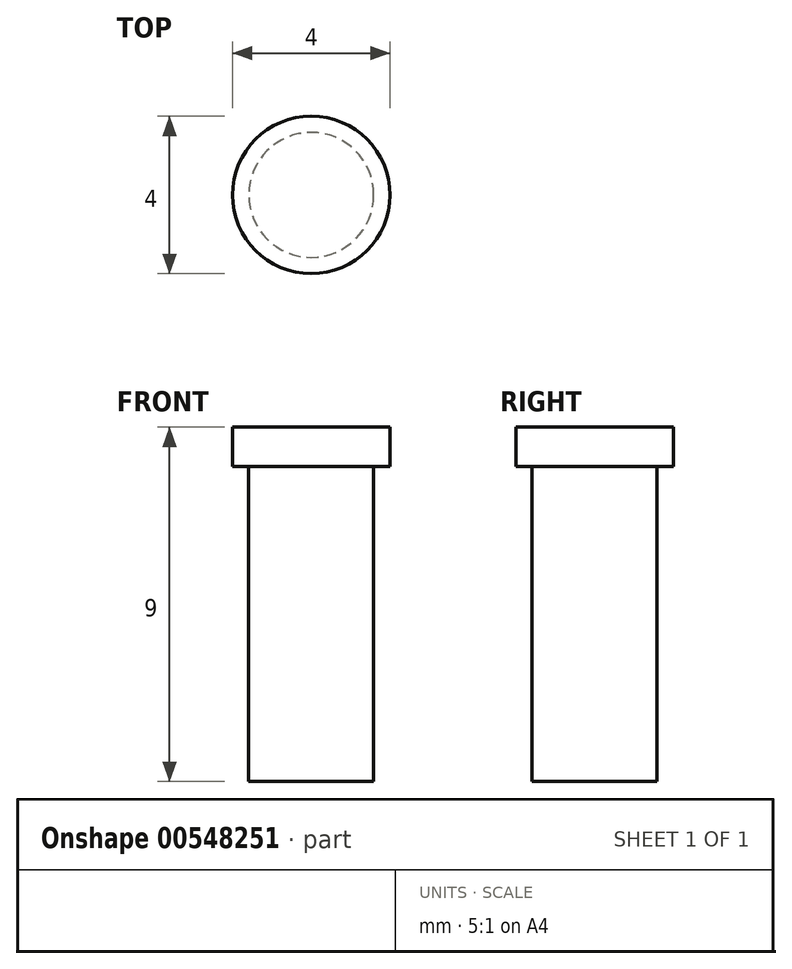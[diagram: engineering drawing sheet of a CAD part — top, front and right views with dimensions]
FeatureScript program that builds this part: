
annotation { "Feature Type Name" : "Feature", "Feature Type Description" : "" }
export const myFeature = defineFeature(function(context is Context, id is Id, definition is map)
    precondition{}
    {
        {
            var Q0;
            Q0=qCreatedBy(makeId("Front.planeOp"),FACE);
            var sketch = newSketch(context, id + "F0", { "sketchPlane" : qUnion([Q0])});
            skLineSegment(sketch, "E0", {"start": v(0, 9.56) * mm, "end": v(0, -1.31) * mm, "construction": true});
            skLineSegment(sketch, "E1", {"start": v(0, 0) * mm, "end": v(-1.59, 0) * mm});
            skLineSegment(sketch, "E2", {"start": v(-1.59, 0) * mm, "end": v(-1.59, 8) * mm});
            skLineSegment(sketch, "E3", {"start": v(-1.59, 8) * mm, "end": v(-2, 8) * mm});
            skLineSegment(sketch, "E4", {"start": v(-2, 8) * mm, "end": v(-2, 9) * mm});
            skLineSegment(sketch, "E5", {"start": v(-2, 9) * mm, "end": v(0, 9) * mm});
            skLineSegment(sketch, "E6", {"start": v(0, 9) * mm, "end": v(0, 0) * mm});
            skSolve(sketch);
        }
        {
            var Q0;
            Q0 = qSketchRegion(id + "F0", true);
            var Q1;
            Q1=sQuery(id+"F0.wireOp",EDGE,"E0");
            revolve(context, id + "F1", {"surfaceOperationType" : NewSurfaceOperationType.NEW, "entities" : qUnion([Q0]), "axis" : qUnion([Q1]), "revolveType" : RevolveType.FULL});
        }
    });
